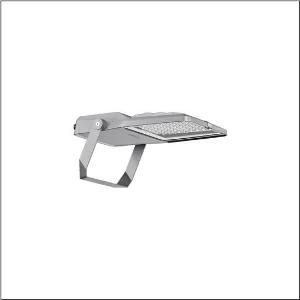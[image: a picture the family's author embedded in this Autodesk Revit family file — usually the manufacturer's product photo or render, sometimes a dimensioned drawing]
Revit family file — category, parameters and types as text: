
# Revit family: floodlight_fl_21_iq_mini___pl61_5xa7772d2c1a_0e67
name_source: partatom
category: Lighting Fixtures
units: mm (PartAtom-declared; Revit-internal decimal feet)

## family parameters
Cut with Voids When Loaded = No
Host = Face
Light Source = No
Part Type = Normal
Room Calculation Point = No
Round Connector Dimension = Use Diameter
Shared = No

## types (1)
- --- (1 x LED, 17500 lm, 143 W, 3000K)
    Apparent Load = 143 VA
    CIE Flux Codes = 33 65 98 100 100
    Color Rendering = 70
    Color Temperature = 3000K
    Default Elevation = 1800 mm
    Description = Floodlight FL 21 iQ mini, floodlight, primary light control with lens, of PMMA, primary optical cover: protective disc, of toughened safety glass, transparent, light distribution: PL61, light emission: direct distribution, installation type: surface-mounted, LED, High Power LED, rated luminous flux: 17.500lm, luminous efficacy: 122lm/W, light colour: 730, colour temperature: 3000K, control: Street-Remote, Auto-Match, Temp-Guard, Night-Set, Smart-Wire, Desk-Remote (wireless, voltage-free reading and setting of iQ features in the workshop via application-optimized NFC function/RFID function), optimised constant luminous flux control (CLO 2.0), with terminal, 6-pole, mains connection: 220..240V, AC, 50/60Hz, start of lifetime: 143W, end of service life: 152W, reduction: 61W, luminaire housing, of diecast aluminium, powder-coated, Siteco® metallic grey (DB 702S), corrosivity category C5 mid according to DIN EN ISO 12944, sealing non-destructively replaceable, mounting bracket, of steel, galvanised, powder-coated, Siteco® metallic grey (DB 702S), protection rating (complete): IP66, insulation class (complete): insulation class II (safety insulation), certification: CE, ENEC, VDE, protection symbol: D, impact resistance: IK08, permissible operating ambient temperature: -40..+40°C, permissible operating ambient temperature for outdoor applications: -40..+50°C, standard: DIN EN 12944, LABS conformity tested according to VDMA 24364:2018-05, packaging unit: 1 piece

Light Distribution: PL61
    Height = 70 mm
    Lamp = 1 x LED
    Lamp Light Flux = 17500 lm
    Lamp Power = 143 W
    Lamp count = 1
    Length = 485 mm
    Luminous efficacy = 122 lm/W
    Manufacturer = Siteco
    ModVariant = No
    Model = 5XA7772D2C1A
    Number of Poles = 1
    OnlyDefault = Yes
    Power Factor = 1
    Product Name = Floodlight FL 21 iQ mini | PL61
    Product group = floodlight | pylon annexe
    ProductGroupID = 6200
    Protection Class = Protection class II
    Protection Degree = IP 66
    RLX_Detail_Level = 1
    RLX_Emergency_Light_Flux = 0 lm
    RLX_Emergency_Type = 0
    RLX_Emergency_Type_DB = No
    RlxData = <blob elided: 96477 chars, md5=82b3542c>
    Socket = socket
    Standby Power = 0 W
    System Light Flux = 17500 lm
    System Power = 143 W
    Type Comments = factory setting: luminous flux: 100 % | dim-lin: 254 | 730 mA
    Type Image = l_1006845.jpg
    URL = http://relux.com
    VarID = @adj_105603
    Voltage = 0 V
    Weight = 0.00 kg
    Width = 337 mm

## geometry (parser evidence)
native form markers: Blend x4, Sweep x13
no freeform markers — native parametric forms only
